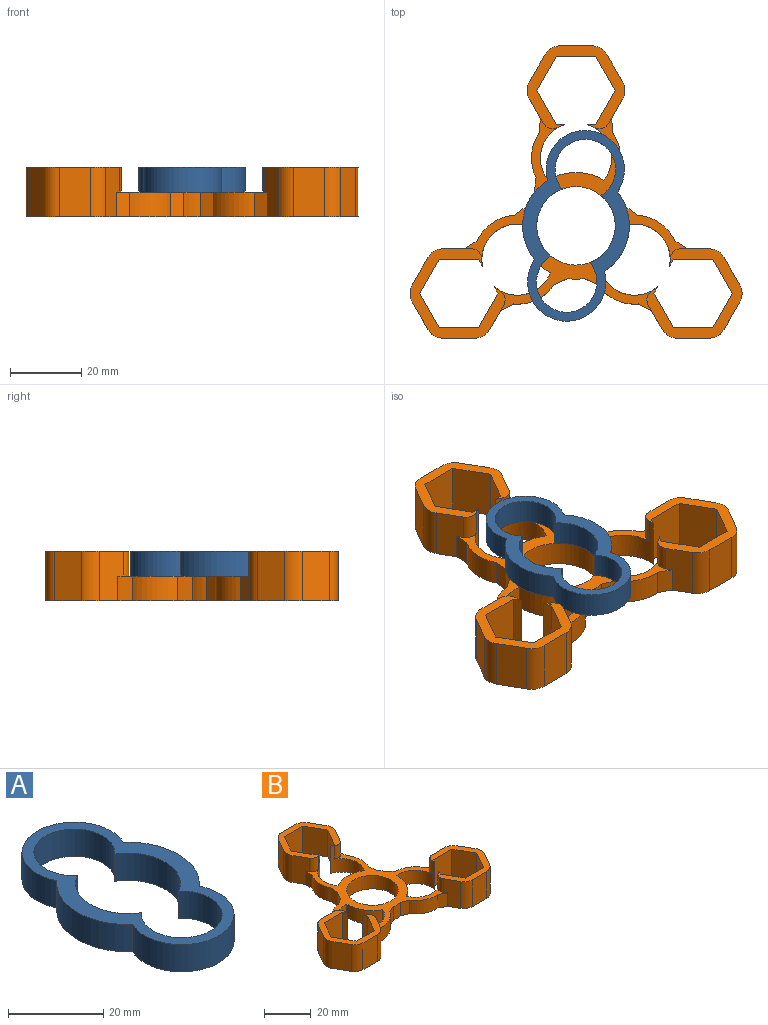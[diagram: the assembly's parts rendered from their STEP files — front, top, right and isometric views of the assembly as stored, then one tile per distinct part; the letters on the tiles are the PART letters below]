
ASSEMBLY  parts=2 mates=1
PART A: 10 faces, bbox 30x54x7 mm
  f0: cylinder r=8.5mm len=17mm, axis (0,0,-1), area 289.6mm2, adj f1,f7,f8,f9
  f1: cylinder r=11.03mm len=19.08mm, axis (0,0,-1), area 161.4mm2, adj f0,f2,f8,f9
  f2: cylinder r=8.5mm len=17mm, axis (0,0,-1), area 289.6mm2, adj f1,f7,f8,f9
  f3: cylinder r=15mm len=22.5mm, axis (0,0,-1), area 178.1mm2, adj f4,f6,f8,f9
  f4: cylinder r=11mm len=22mm, axis (0,0,-1), area 310.7mm2, adj f3,f5,f8,f9
  f5: cylinder r=15mm len=22.5mm, axis (0,0,-1), area 178.1mm2, adj f4,f6,f8,f9
  f6: cylinder r=11mm len=22mm, axis (0,0,-1), area 310.7mm2, adj f3,f5,f8,f9
  f7: cylinder r=11.03mm len=19.08mm, axis (0,0,-1), area 161.4mm2, adj f0,f2,f8,f9
  f8: plane 54x30mm, normal (0,0,1), area 404.5mm2, adj f0,f1,f2,f3,f4,f5,f6,f7
  f9: plane 54x30mm, normal (0,0,-1), area 404.5mm2, adj f0,f1,f2,f3,f4,f5,f6,f7
PART B: 90 faces, bbox 93.2x82.1x14 mm
  f0: cylinder r=15mm len=7mm, axis (0,0,-1), area 32.3mm2, adj f19,f20,f64,f65
  f1: cylinder r=12.5mm len=10.48mm, axis (0,0,-1), area 93.3mm2, adj f19,f20,f65,f66
  f2: cylinder r=10mm len=14mm, axis (0,0,-1), area 147.2mm2, adj f3,f19,f20,f38,f46,f89
  f3: cylinder r=15mm len=13.58mm, axis (0,0,-1), area 115.5mm2, adj f2,f4,f19,f20
  f4: cylinder r=10mm len=15.85mm, axis (0,0,-1), area 147.2mm2, adj f3,f19,f20,f42,f46,f88
  f5: cylinder r=12.5mm len=11.47mm, axis (0,0,-1), area 93.3mm2, adj f19,f20,f63,f71
  f6: cylinder r=15mm len=7mm, axis (0,0,-1), area 32.3mm2, adj f19,f20,f62,f63
  f7: cylinder r=12.5mm len=11.47mm, axis (0,0,-1), area 93.3mm2, adj f19,f20,f62,f70
  f8: cylinder r=10mm len=15.85mm, axis (0,0,-1), area 147.2mm2, adj f9,f19,f20,f51,f59,f86
  f9: cylinder r=15mm len=13.58mm, axis (0,0,-1), area 115.5mm2, adj f8,f10,f19,f20
  f10: cylinder r=10mm len=14mm, axis (0,0,-1), area 147.2mm2, adj f9,f19,f20,f55,f59,f87
  f11: cylinder r=12.5mm len=10.48mm, axis (0,0,-1), area 93.3mm2, adj f19,f20,f60,f69
  f12: cylinder r=15mm len=7mm, axis (0,0,-1), area 32.3mm2, adj f19,f20,f60,f61
  f13: cylinder r=12.5mm len=12.67mm, axis (0,0,-1), area 93.3mm2, adj f19,f20,f61,f68
  f14: cylinder r=10mm len=15.66mm, axis (0,0,-1), area 147.2mm2, adj f15,f19,f20,f24,f33,f85
  f15: cylinder r=15mm len=15.68mm, axis (0,0,-1), area 115.5mm2, adj f14,f16,f19,f20
  f16: cylinder r=10mm len=15.66mm, axis (0,0,-1), area 147.2mm2, adj f15,f19,f20,f28,f33,f84
  f17: cylinder r=12.5mm len=12.67mm, axis (0,0,-1), area 93.3mm2, adj f19,f20,f64,f67
  f18: cylinder r=11.03mm len=22.05mm, axis (0,0,-1), area 484.9mm2, adj f19,f20
  f19: plane 62.55x54.17mm, normal (0,0,1), area 617.8mm2, adj f0,f1,f2,f3,f4,f5,f6,f7
  f20: plane 93.25x82.1mm, normal (0,0,-1), area 1170.7mm2, adj f0,f1,f2,f3,f4,f5,f6,f7
  f21: plane 14x6.77mm, normal (0.87,-0.5,0), area 96.6mm2, adj f19,f20,f33,f68,f75,f85
  f22: plane 14x6.77mm, normal (-0.87,-0.5,0), area 96.6mm2, adj f19,f20,f33,f67,f72,f84
  f23: plane 14x9.55mm, normal (-0.87,0.5,0), area 154.3mm2, adj f20,f24,f32,f33
  f24: plane 14x2.25mm, normal (0,1,0), area 31.5mm2, adj f14,f20,f23,f33
  f25: plane 14x7.55mm, normal (0.87,0.5,0), area 122mm2, adj f20,f33,f74,f75
  f26: plane 14x8.72mm, normal (0,1,0), area 122mm2, adj f20,f33,f73,f74
  f27: plane 14x7.55mm, normal (-0.87,0.5,0), area 122mm2, adj f20,f33,f72,f73
  f28: plane 14x2.25mm, normal (0,1,0), area 31.5mm2, adj f16,f20,f29,f33
  f29: plane 14x9.55mm, normal (0.87,0.5,0), area 154.3mm2, adj f20,f28,f30,f33
  f30: plane 14x9.55mm, normal (0.87,-0.5,0), area 154.3mm2, adj f20,f29,f31,f33
  f31: plane 14x11.03mm, normal (0,-1,0), area 154.4mm2, adj f20,f30,f32,f33
  f32: plane 14x9.55mm, normal (-0.87,-0.5,0), area 154.3mm2, adj f20,f23,f31,f33
  f33: plane 27.43x23.31mm, normal (0,0,1), area 184.3mm2, adj f14,f16,f21,f22,f23,f24,f25,f26
  f34: plane 14x7.81mm, normal (0,1,0), area 96.6mm2, adj f19,f20,f46,f66,f83,f89
  f35: plane 14x6.77mm, normal (0.87,-0.5,0), area 96.6mm2, adj f19,f20,f46,f71,f80,f88
  f36: plane 14x9.55mm, normal (0.87,-0.5,0), area 154.3mm2, adj f20,f37,f45,f46
  f37: plane 14x11.03mm, normal (0,-1,0), area 154.4mm2, adj f20,f36,f38,f46
  f38: plane 14x1.95mm, normal (-0.87,-0.5,0), area 31.5mm2, adj f2,f20,f37,f46
  f39: plane 14x7.55mm, normal (-0.87,0.5,0), area 122mm2, adj f20,f46,f82,f83
  f40: plane 14x7.55mm, normal (-0.87,-0.5,0), area 122mm2, adj f20,f46,f81,f82
  f41: plane 14x8.72mm, normal (0,-1,0), area 122mm2, adj f20,f46,f80,f81
  f42: plane 14x1.95mm, normal (-0.87,-0.5,0), area 31.5mm2, adj f4,f20,f43,f46
  f43: plane 14x9.55mm, normal (-0.87,0.5,0), area 154.3mm2, adj f20,f42,f44,f46
  f44: plane 14x11.03mm, normal (0,1,0), area 154.4mm2, adj f20,f43,f45,f46
  f45: plane 14x9.55mm, normal (0.87,0.5,0), area 154.3mm2, adj f20,f36,f44,f46
  f46: plane 26.71x25.1mm, normal (0,0,1), area 184.3mm2, adj f2,f4,f34,f35,f36,f37,f38,f39
  f47: plane 14x7.81mm, normal (0,1,0), area 96.6mm2, adj f19,f20,f59,f69,f79,f87
  f48: plane 14x6.77mm, normal (-0.87,-0.5,0), area 96.6mm2, adj f19,f20,f59,f70,f76,f86
  f49: plane 14x11.03mm, normal (0,1,0), area 154.4mm2, adj f20,f50,f58,f59
  f50: plane 14x9.55mm, normal (0.87,0.5,0), area 154.3mm2, adj f20,f49,f51,f59
  f51: plane 14x1.95mm, normal (0.87,-0.5,0), area 31.5mm2, adj f8,f20,f50,f59
  f52: plane 14x8.72mm, normal (0,-1,0), area 122mm2, adj f20,f59,f76,f77
  f53: plane 14x7.55mm, normal (0.87,-0.5,0), area 122mm2, adj f20,f59,f77,f78
  f54: plane 14x7.55mm, normal (0.87,0.5,0), area 122mm2, adj f20,f59,f78,f79
  f55: plane 14x1.95mm, normal (0.87,-0.5,0), area 31.5mm2, adj f10,f20,f56,f59
  f56: plane 14x11.03mm, normal (0,-1,0), area 154.4mm2, adj f20,f55,f57,f59
  f57: plane 14x9.55mm, normal (-0.87,-0.5,0), area 154.3mm2, adj f20,f56,f58,f59
  f58: plane 14x9.55mm, normal (-0.87,0.5,0), area 154.3mm2, adj f20,f49,f57,f59
  f59: plane 26.71x25.1mm, normal (0,0,1), area 184.3mm2, adj f8,f10,f47,f48,f49,f50,f51,f52
  f60: plane 7x3.32mm, normal (0.59,0.81,0), area 28.9mm2, adj f11,f12,f19,f20
  f61: plane 7x4.1mm, normal (0.99,0.11,0), area 28.9mm2, adj f12,f13,f19,f20
  f62: plane 7x3.78mm, normal (-0.4,-0.92,0), area 28.9mm2, adj f6,f7,f19,f20
  f63: plane 7x3.78mm, normal (0.4,-0.92,0), area 28.9mm2, adj f5,f6,f19,f20
  f64: plane 7x4.1mm, normal (-0.99,0.11,0), area 28.9mm2, adj f0,f17,f19,f20
  f65: plane 7x3.32mm, normal (-0.59,0.81,0), area 28.9mm2, adj f0,f1,f19,f20
  f66: plane 7x3.49mm, normal (-0.54,0.84,0), area 29mm2, adj f1,f19,f20,f34
  f67: plane 7x4.13mm, normal (-1,0.04,0), area 29mm2, adj f17,f19,f20,f22
  f68: plane 7x4.13mm, normal (1,0.04,0), area 29mm2, adj f13,f19,f20,f21
  f69: plane 7x3.49mm, normal (0.54,0.84,0), area 29mm2, adj f11,f19,f20,f47
  f70: plane 7x3.67mm, normal (-0.46,-0.89,0), area 29mm2, adj f7,f19,f20,f48
  f71: plane 7x3.67mm, normal (0.46,-0.89,0), area 29mm2, adj f5,f19,f20,f35
  f72: cylinder r=5mm len=14mm, axis (0,0,-1), area 73.3mm2, adj f20,f22,f27,f33
  f73: cylinder r=5mm len=14mm, axis (0,0,-1), area 73.3mm2, adj f20,f26,f27,f33
  f74: cylinder r=5mm len=14mm, axis (0,0,-1), area 73.3mm2, adj f20,f25,f26,f33
  f75: cylinder r=5mm len=14mm, axis (0,0,-1), area 73.3mm2, adj f20,f21,f25,f33
  f76: cylinder r=5mm len=14mm, axis (0,0,-1), area 73.3mm2, adj f20,f48,f52,f59
  f77: cylinder r=5mm len=14mm, axis (0,0,-1), area 73.3mm2, adj f20,f52,f53,f59
  f78: cylinder r=5mm len=14mm, axis (0,0,-1), area 73.3mm2, adj f20,f53,f54,f59
  f79: cylinder r=5mm len=14mm, axis (0,0,-1), area 73.3mm2, adj f20,f47,f54,f59
  f80: cylinder r=5mm len=14mm, axis (0,0,-1), area 73.3mm2, adj f20,f35,f41,f46
  f81: cylinder r=5mm len=14mm, axis (0,0,-1), area 73.3mm2, adj f20,f40,f41,f46
  f82: cylinder r=5mm len=14mm, axis (0,0,-1), area 73.3mm2, adj f20,f39,f40,f46
  f83: cylinder r=5mm len=14mm, axis (0,0,-1), area 73.3mm2, adj f20,f34,f39,f46
  f84: cylinder r=3mm len=7mm, axis (0,0,-1), area 33.1mm2, adj f16,f19,f22,f33
  f85: cylinder r=3mm len=7mm, axis (0,0,-1), area 33.1mm2, adj f14,f19,f21,f33
  f86: cylinder r=3mm len=7mm, axis (0,0,-1), area 33.1mm2, adj f8,f19,f48,f59
  f87: cylinder r=3mm len=7mm, axis (0,0,-1), area 33.1mm2, adj f10,f19,f47,f59
  f88: cylinder r=3mm len=7mm, axis (0,0,-1), area 33.1mm2, adj f4,f19,f35,f46
  f89: cylinder r=3mm len=7mm, axis (0,0,-1), area 33.1mm2, adj f2,f19,f34,f46
PLACE A rot(axis=(1,-0.08,0),180deg) t=(56.13,18.37,0.19)mm
PLACE B t=(56.13,18.37,-13.81)mm fixed
MATE revolute A.f1 <-> B.f0  axis (0,0,-1) through (56.13,18.37,-6.81)mm
